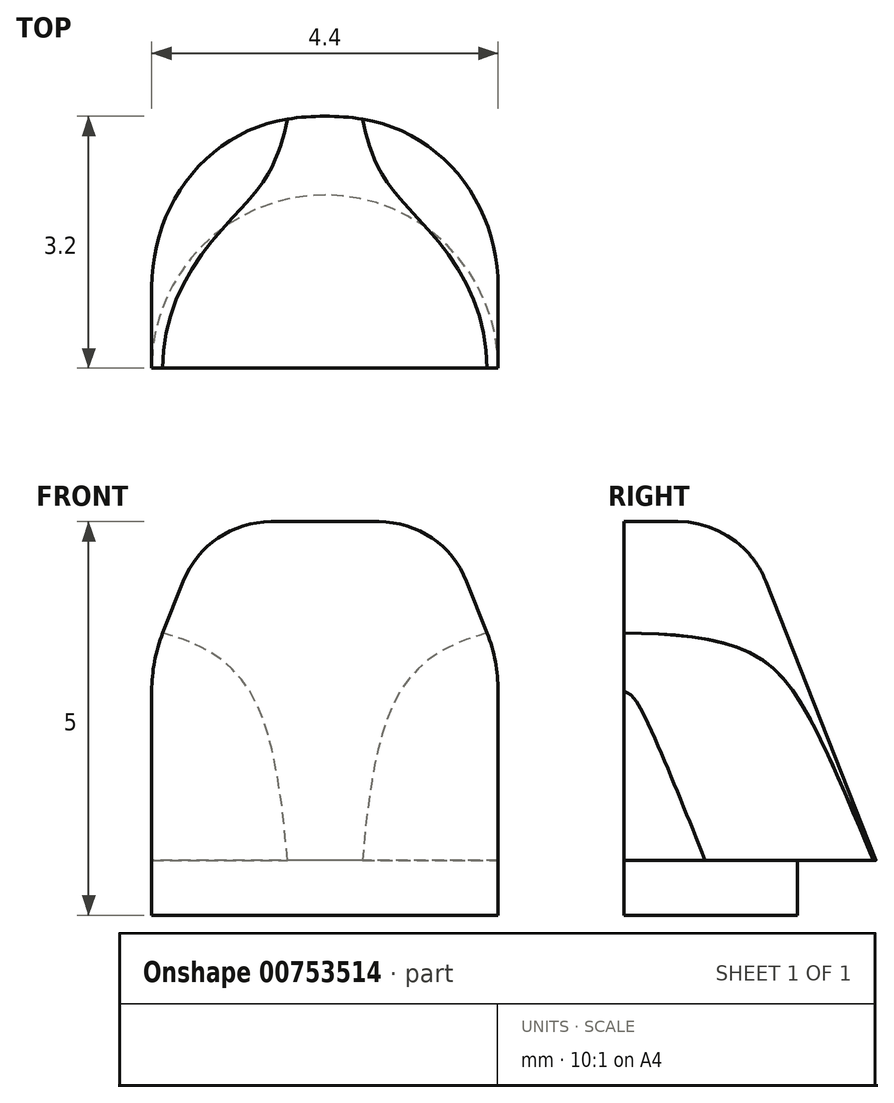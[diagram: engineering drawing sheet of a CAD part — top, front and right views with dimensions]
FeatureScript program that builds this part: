
annotation { "Feature Type Name" : "Feature", "Feature Type Description" : "" }
export const myFeature = defineFeature(function(context is Context, id is Id, definition is map)
    precondition{}
    {
        {
            var Q0;
            Q0=qCreatedBy(makeId("Front.planeOp"),FACE);
            var sketch = newSketch(context, id + "F0", { "sketchPlane" : qUnion([Q0])});
            skLineSegment(sketch, "E0", {"start": v(-2.2, 0.7) * mm, "end": v(-2.2, 0) * mm});
            skLineSegment(sketch, "E1", {"start": v(-2.2, 0) * mm, "end": v(0, 0) * mm});
            skLineSegment(sketch, "E2", {"start": v(0, 0) * mm, "end": v(0, 5) * mm});
            skLineSegment(sketch, "E3", {"start": v(0, 5) * mm, "end": v(-0.68, 5) * mm});
            skLineSegment(sketch, "E4", {"start": v(-1.8, 4.24) * mm, "end": v(-3.2, 0.7) * mm});
            skLineSegment(sketch, "E5", {"start": v(-3.2, 0.7) * mm, "end": v(-2.2, 0.7) * mm});
            skLineSegment(sketch, "E6", {"start": v(0, 6) * mm, "end": v(0, -6) * mm, "construction": true});
            skPoint(sketch, "E7.visualSharp", {"position": v(-1.5, 5) * mm});
            skArc(sketch, "E7.filletArc", {"start": v(-0.68, 5) * mm, "mid": v(-1.36, 4.8) * mm, "end": v(-1.8, 4.24) * mm});
            skSolve(sketch);
        }
        {
            var Q0;
            Q0=makeQuery(id+"F0.imprint","IMPRINT",FACE,{"disambiguationData":[TD([[makeQuery(id+"F0.imprint","IMPRINT",EDGE,{"derivedFrom":sQuery(id+"F0.wireOp",EDGE,"E0")}),1.0]])]});
            var Q1;
            Q1=sQuery(id+"F0.wireOp",EDGE,"E6");
            revolve(context, id + "F1", {"surfaceOperationType" : NewSurfaceOperationType.NEW, "entities" : qUnion([Q0]), "axis" : qUnion([Q1]), "revolveType" : RevolveType.ONE_DIRECTION, "angle" : 180 * degree});
        }
        {
            var Q0;
            Q0=qCreatedBy(makeId("Front.planeOp"),FACE);
            var sketch = newSketch(context, id + "F2", { "sketchPlane" : qUnion([Q0])});
            skLineSegment(sketch, "E8.bottom", {"start": v(-2.2, 0) * mm, "end": v(-3.7, 0) * mm});
            skLineSegment(sketch, "E8.top", {"start": v(-2.2, 4) * mm, "end": v(-3.7, 4) * mm});
            skLineSegment(sketch, "E8.left", {"start": v(-2.2, 0) * mm, "end": v(-2.2, 4) * mm});
            skLineSegment(sketch, "E8.right", {"start": v(-3.7, 0) * mm, "end": v(-3.7, 4) * mm});
            skLineSegment(sketch, "E9.MirrorCS", {"start": v(2.2, 4) * mm, "end": v(3.7, 4) * mm});
            skLineSegment(sketch, "E10.MirrorCS", {"start": v(2.2, 0) * mm, "end": v(2.2, 4) * mm});
            skLineSegment(sketch, "E11.MirrorCS", {"start": v(3.7, 0) * mm, "end": v(3.7, 4) * mm});
            skLineSegment(sketch, "E12.MirrorCS", {"start": v(2.2, 0) * mm, "end": v(3.7, 0) * mm});
            skSolve(sketch);
        }
        {
            var Q0;
            Q0 = qSketchRegion(id + "F2", true);
            extrude(context, id + "F3", {"entities" : qUnion([Q0]), "operationType" : NewBodyOperationType.REMOVE, "oppositeDirection" : true, "depth" : 25 * mm, "offsetDistance" : 25 * mm});
        }
        {
            var Q0;
            Q0=makeQuery(id+"F3.boolean.opBoolean","INTERSECT",EDGE,{"derivedFrom":[makeQuery(id+"F1.opRevolve","SWEPT_FACE",FACE,{"disambiguationData":[OSD([sQuery(id+"F0.wireOp",EDGE,"E4")])]}),makeQuery(id+"F3.opExtrude","SWEPT_FACE",FACE,{"disambiguationData":[OSD([sQuery(id+"F2.wireOp",EDGE,"E8.left")])]})]});
            var Q1;
            Q1=makeQuery(id+"F3.boolean.opBoolean","INTERSECT",EDGE,{"derivedFrom":[makeQuery(id+"F1.opRevolve","SWEPT_FACE",FACE,{"disambiguationData":[OSD([sQuery(id+"F0.wireOp",EDGE,"E4")])]}),makeQuery(id+"F3.opExtrude","SWEPT_FACE",FACE,{"disambiguationData":[OSD([sQuery(id+"F2.wireOp",EDGE,"E10.MirrorCS")])]})]});
            fillet(context, id + "F4", {"entities" : qUnion([Q0, Q1]), "radius" : 2 * mm, "tangentPropagation" : true, "allowEdgeOverflow" : false});
        }
    });
